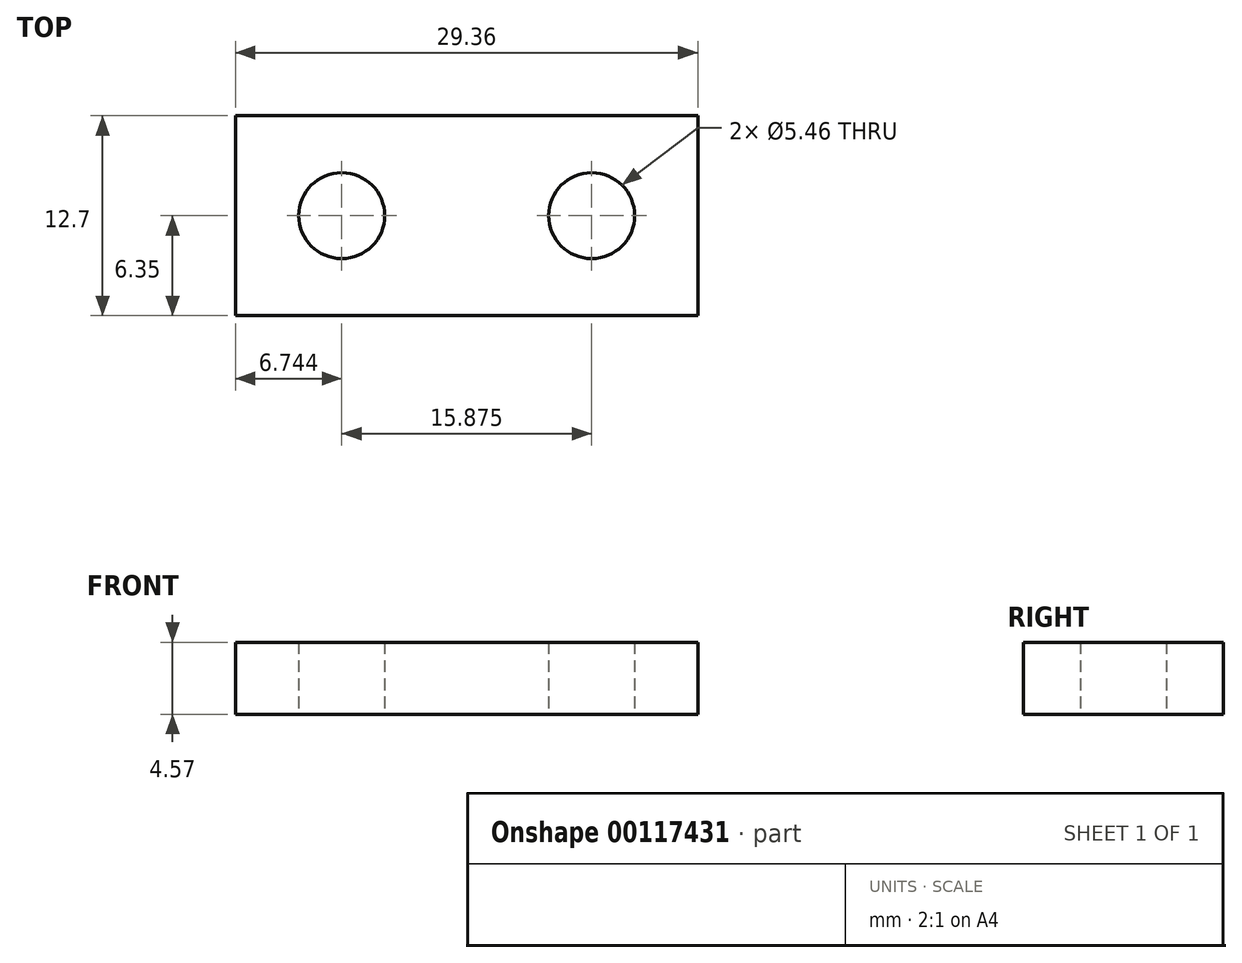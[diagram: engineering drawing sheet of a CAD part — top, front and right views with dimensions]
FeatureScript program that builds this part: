
annotation { "Feature Type Name" : "Feature", "Feature Type Description" : "" }
export const myFeature = defineFeature(function(context is Context, id is Id, definition is map)
    precondition{}
    {
        {
            var Q0;
            Q0=qCreatedBy(makeId("Top.planeOp"),FACE);
            var sketch = newSketch(context, id + "F0", { "sketchPlane" : qUnion([Q0])});
            skLineSegment(sketch, "E0.bottom", {"start": v(0, 0) * mm, "end": v(29.36, 0) * mm});
            skLineSegment(sketch, "E0.top", {"start": v(0, 12.7) * mm, "end": v(29.36, 12.7) * mm});
            skLineSegment(sketch, "E0.left", {"start": v(0, 0) * mm, "end": v(0, 12.7) * mm});
            skLineSegment(sketch, "E0.right", {"start": v(29.36, 0) * mm, "end": v(29.36, 12.7) * mm});
            skCircle(sketch, "E1", {"center": v(6.74, 6.35) * mm, "radius": 2.73 * mm});
            skCircle(sketch, "E2", {"center": v(22.62, 6.35) * mm, "radius": 2.73 * mm});
            skCircle(sketch, "E3", {"center": v(6.74, 6.35) * mm, "radius": 5.16 * mm, "construction": true});
            skSolve(sketch);
        }
        {
            var Q0;
            Q0 = qSketchRegion(id + "F0", true);
            extrude(context, id + "F1", {"entities" : qUnion([Q0]), "depth" : 4.57 * mm});
        }
    });
